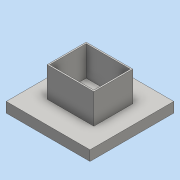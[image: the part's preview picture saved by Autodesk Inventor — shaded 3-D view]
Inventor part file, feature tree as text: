
AUTODESK INVENTOR PART (.ipt)
format: ipt  version: 2016 (Build 200138000, 138)  size: 88,064 bytes
history: native  units: mm
features: extrude x2, sketch x2
ambient origin geometry x8: Origin, YZ Plane, XZ Plane, XY Plane, X Axis, Y Axis, Z Axis, Center Point
bodies: Solid1 (feature_tree)
feature tree (4):
  extrude  "Extrusion1"  Depth=34.3mm
  extrude  "Extrusion2"  Depth=18.05mm
  sketch  "Sketch1"  dims[d0=34.3mm d1=34.3mm]
  sketch  "Sketch2"  dims[d2=4.15mm d3=0.0mm d4=18.05mm d5=14.9mm d6=12.25mm d7=0.0mm]
